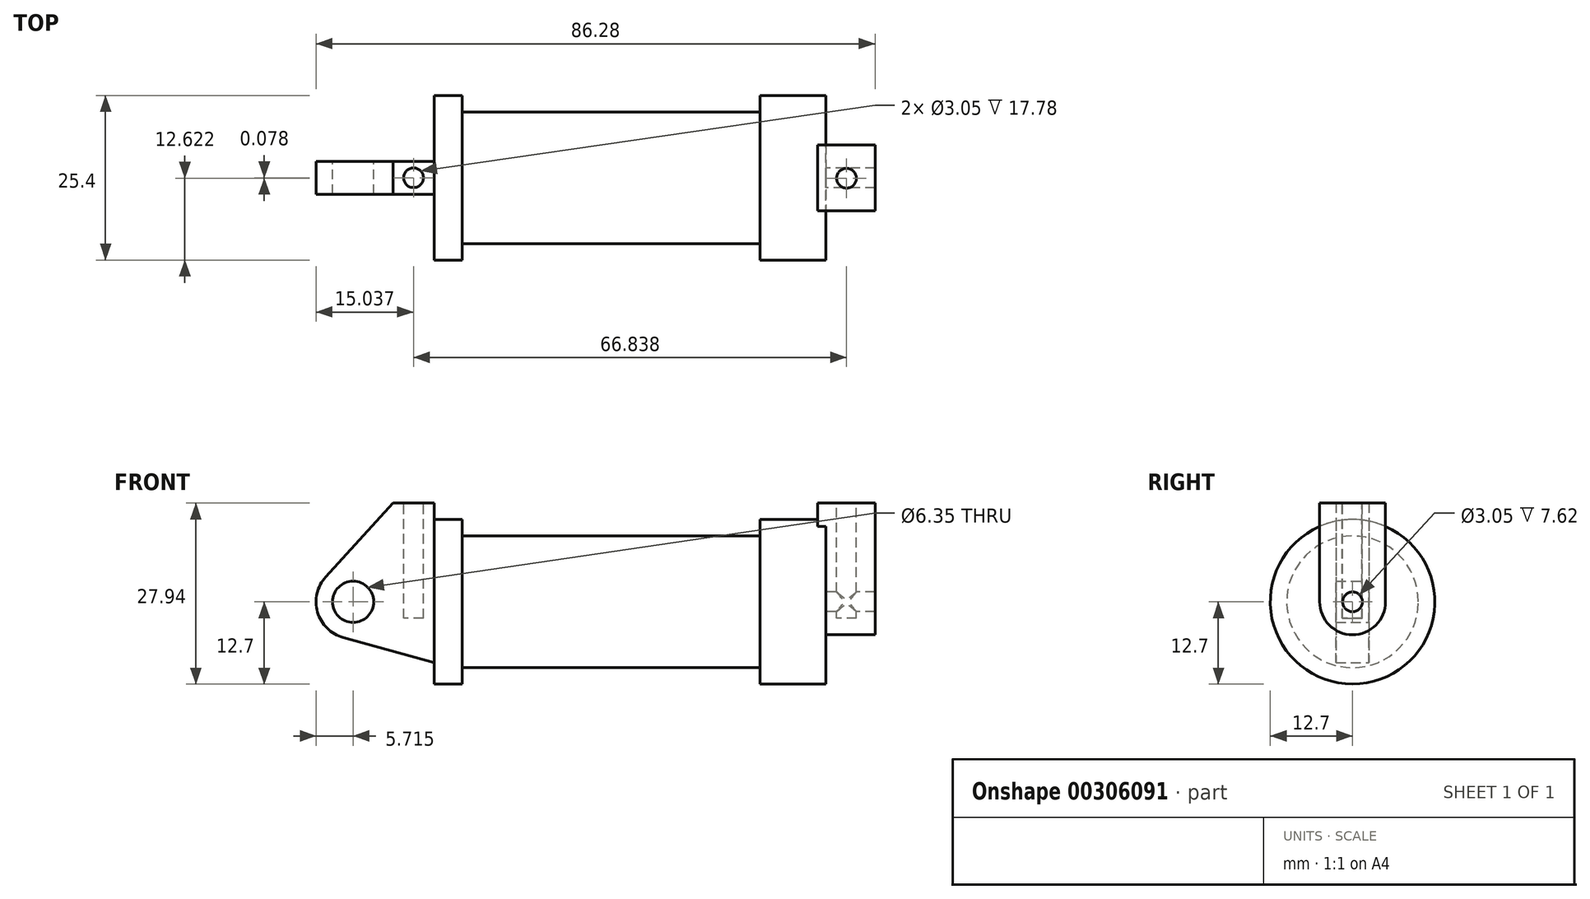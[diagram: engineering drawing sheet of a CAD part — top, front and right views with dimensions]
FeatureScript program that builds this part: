
annotation { "Feature Type Name" : "Feature", "Feature Type Description" : "" }
export const myFeature = defineFeature(function(context is Context, id is Id, definition is map)
    precondition{}
    {
        {
            var Q0;
            Q0=qCreatedBy(makeId("Front.planeOp"),FACE);
            var sketch = newSketch(context, id + "F0", { "sketchPlane" : qUnion([Q0])});
            skLineSegment(sketch, "E0", {"start": v(0, 0) * mm, "end": v(0, 12.7) * mm});
            skLineSegment(sketch, "E1", {"start": v(0, 12.7) * mm, "end": v(10.16, 12.7) * mm});
            skLineSegment(sketch, "E2", {"start": v(10.16, 12.7) * mm, "end": v(10.16, 10.16) * mm});
            skLineSegment(sketch, "E3", {"start": v(10.16, 10.16) * mm, "end": v(56.13, 10.16) * mm});
            skLineSegment(sketch, "E4", {"start": v(56.13, 10.16) * mm, "end": v(56.13, 12.7) * mm});
            skLineSegment(sketch, "E5", {"start": v(56.13, 12.7) * mm, "end": v(66.3, 12.7) * mm});
            skLineSegment(sketch, "E6", {"start": v(66.3, 12.7) * mm, "end": v(66.3, 0) * mm});
            skLineSegment(sketch, "E7", {"start": v(66.3, 0) * mm, "end": v(0, 0) * mm});
            skLineSegment(sketch, "E8", {"start": v(5.84, 15.24) * mm, "end": v(-0.5, 15.24) * mm});
            skLineSegment(sketch, "E9", {"start": v(-0.5, 15.24) * mm, "end": v(-10.88, 3.85) * mm});
            skLineSegment(sketch, "E10", {"start": v(0, 0) * mm, "end": v(-6.65, 0) * mm});
            skCircle(sketch, "E11", {"center": v(-6.65, 0) * mm, "radius": 5.72 * mm});
            skCircle(sketch, "E12", {"center": v(-6.65, 0) * mm, "radius": 3.18 * mm});
            skLineSegment(sketch, "E13", {"start": v(5.84, 15.24) * mm, "end": v(5.84, -9.4) * mm});
            skLineSegment(sketch, "E14", {"start": v(5.84, -9.4) * mm, "end": v(-8.18, -5.5) * mm});
            skSolve(sketch);
        }
        {
            var Q0;
            {var subQ0=sQuery(id+"F0.wireOp",EDGE,"E2");Q0=makeQuery(id+"F0.imprint","IMPRINT",FACE,{"disambiguationData":[TD([[makeQuery(id+"F0.imprint","IMPRINT",EDGE,{"derivedFrom":subQ0}),-1.0]])]});}
            var Q1;
            Q1=sQuery(id+"F0.wireOp",EDGE,"E7");
            revolve(context, id + "F1", {"entities" : qUnion([Q0]), "axis" : qUnion([Q1]), "revolveType" : RevolveType.FULL});
        }
        {
            var Q0;
            {var subQ0=sQuery(id+"F0.wireOp",EDGE,"E14");Q0=makeQuery(id+"F0.imprint","IMPRINT",FACE,{"disambiguationData":[TD([[makeQuery(id+"F0.imprint","IMPRINT",EDGE,{"derivedFrom":subQ0}),-1.0]])]});}
            var Q1;
            Q1=makeQuery(id+"F0.imprint","IMPRINT",FACE,{"disambiguationData":[TD([[makeQuery(id+"F0.imprint","IMPRINT",EDGE,{"derivedFrom":sQuery(id+"F0.wireOp",EDGE,"E12")}),-1.0]])]});
            var Q2;
            {var subQ1=sQuery(id+"F0.wireOp",EDGE,"E0");Q2=makeQuery(id+"F0.imprint","IMPRINT",FACE,{"disambiguationData":[TD([[makeQuery(id+"F0.imprint","IMPRINT",EDGE,{"derivedFrom":subQ1}),1.0]])]});}
            var Q3;
            {var subQ0=sQuery(id+"F0.wireOp",EDGE,"E0");Q3=makeQuery(id+"F0.imprint","IMPRINT",FACE,{"disambiguationData":[TD([[makeQuery(id+"F0.imprint","IMPRINT",EDGE,{"derivedFrom":subQ0}),-1.0]])]});}
            extrude(context, id + "F2", {"entities" : qUnion([Q0, Q1, Q2, Q3]), "operationType" : NewBodyOperationType.ADD, "endBound" : BoundingType.SYMMETRIC, "depth" : 5.08 * mm});
        }
        {
            var Q0;
            Q0=makeQuery(id+"F1.opRevolve","SWEPT_FACE",FACE,{"disambiguationData":[OSD([sQuery(id+"F0.wireOp",EDGE,"E6")])]});
            var sketch = newSketch(context, id + "F3", { "sketchPlane" : qUnion([Q0])});
            skCircle(sketch, "E15", {"center": v(0, 0) * mm, "radius": 1.52 * mm});
            skCircle(sketch, "E16", {"center": v(0, 0) * mm, "radius": 5.08 * mm});
            skLineSegment(sketch, "E17", {"start": v(0, 0) * mm, "end": v(-5.08, 0) * mm, "construction": true});
            skLineSegment(sketch, "E18", {"start": v(0, 0) * mm, "end": v(5.08, 0) * mm, "construction": true});
            skLineSegment(sketch, "E19", {"start": v(-5.08, 0) * mm, "end": v(-5.08, 15.24) * mm});
            skLineSegment(sketch, "E20", {"start": v(5.08, 0) * mm, "end": v(5.08, 15.24) * mm});
            skLineSegment(sketch, "E21", {"start": v(-5.08, 15.24) * mm, "end": v(5.08, 15.24) * mm});
            skSolve(sketch);
        }
        {
            var Q0;
            Q0=makeQuery(id+"F3.imprint","IMPRINT",FACE,{"disambiguationData":[TD([[makeQuery(id+"F3.imprint","IMPRINT",EDGE,{"derivedFrom":sQuery(id+"F3.wireOp",EDGE,"E15")}),-1.0]])]});
            var Q1;
            {var subQ0=sQuery(id+"F3.wireOp",EDGE,"E19");var subQ1=sQuery(id+"F3.wireOp",EDGE,"E16");var subQ2=makeQuery(id+"F3.imprint","INTERSECT",VERTEX,{"derivedFrom":[subQ1,subQ0]});Q1=makeQuery(id+"F3.imprint","IMPRINT",FACE,{"disambiguationData":[TD([[makeQuery(id+"F3.imprint","IMPRINT",EDGE,{"disambiguationData":[TD([[subQ2,1.0]])],"derivedFrom":subQ1}),-1.0]])]});}
            var Q2;
            {var subQ0=sQuery(id+"F3.wireOp",EDGE,"E21");Q2=makeQuery(id+"F3.imprint","IMPRINT",FACE,{"disambiguationData":[TD([[makeQuery(id+"F3.imprint","IMPRINT",EDGE,{"derivedFrom":subQ0}),-1.0]])]});}
            extrude(context, id + "F4", {"entities" : qUnion([Q0, Q1, Q2]), "operationType" : NewBodyOperationType.ADD, "depth" : 7.62 * mm, "hasSecondDirection" : true, "secondDirectionOppositeDirection" : true, "secondDirectionDepth" : 1.27 * mm});
        }
        {
            var Q0;
            Q0=makeQuery(id+"F2.opExtrude","SWEPT_FACE",FACE,{"disambiguationData":[OSD([sQuery(id+"F0.wireOp",EDGE,"E8")])]});
            var sketch = newSketch(context, id + "F5", { "sketchPlane" : qUnion([Q0])});
            skLineSegment(sketch, "E22", {"start": v(-0.5, 0) * mm, "end": v(5.84, 0) * mm, "construction": true});
            skCircle(sketch, "E23", {"center": v(2.67, 0) * mm, "radius": 1.52 * mm});
            skLineSegment(sketch, "E24", {"start": v(65.04, -0.08) * mm, "end": v(73.97, -0.08) * mm, "construction": true});
            skCircle(sketch, "E25", {"center": v(69.5, -0.08) * mm, "radius": 1.52 * mm});
            skSolve(sketch);
        }
        {
            var Q0;
            Q0=makeQuery(id+"F5.imprint","IMPRINT",FACE,{"disambiguationData":[TD([[makeQuery(id+"F5.imprint","IMPRINT",EDGE,{"derivedFrom":sQuery(id+"F5.wireOp",EDGE,"E23")}),1.0]])]});
            var Q1;
            Q1=makeQuery(id+"F5.imprint","IMPRINT",FACE,{"disambiguationData":[TD([[makeQuery(id+"F5.imprint","IMPRINT",EDGE,{"derivedFrom":sQuery(id+"F5.wireOp",EDGE,"E25")}),1.0]])]});
            extrude(context, id + "F6", {"entities" : qUnion([Q0, Q1]), "operationType" : NewBodyOperationType.REMOVE, "oppositeDirection" : true, "depth" : 17.78 * mm});
        }
    });
